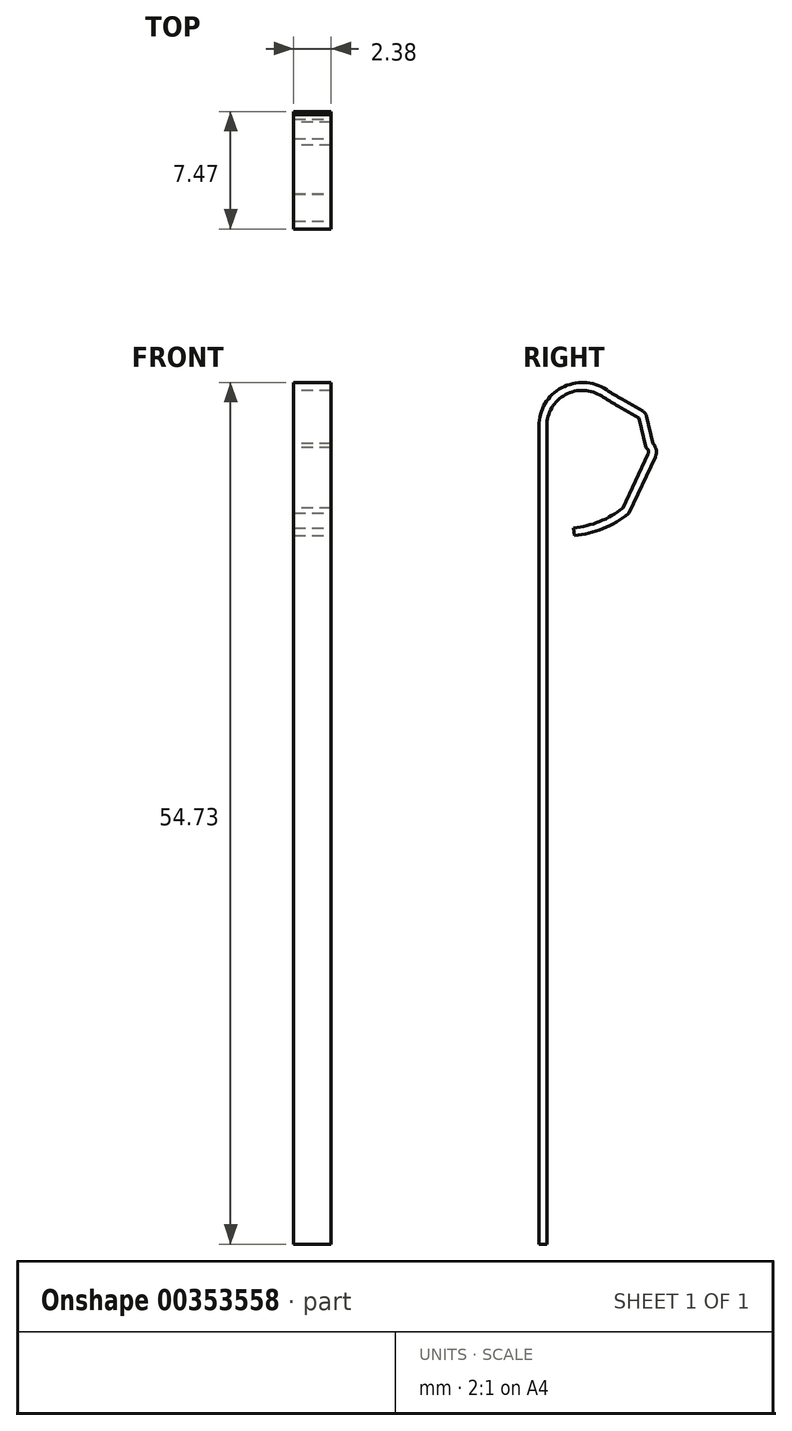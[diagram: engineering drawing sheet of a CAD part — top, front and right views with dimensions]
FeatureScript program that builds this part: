
annotation { "Feature Type Name" : "Feature", "Feature Type Description" : "" }
export const myFeature = defineFeature(function(context is Context, id is Id, definition is map)
    precondition{}
    {
        {
            var Q0;
            Q0=qCreatedBy(makeId("Top.planeOp"),FACE);
            var sketch = newSketch(context, id + "F0", { "sketchPlane" : qUnion([Q0])});
            skLineSegment(sketch, "E0.bottom", {"start": v(-1.2, 0.25) * mm, "end": v(1.2, 0.25) * mm});
            skLineSegment(sketch, "E0.top", {"start": v(-1.2, -0.25) * mm, "end": v(1.2, -0.25) * mm});
            skLineSegment(sketch, "E0.left", {"start": v(-1.2, 0.25) * mm, "end": v(-1.2, -0.25) * mm});
            skLineSegment(sketch, "E0.right", {"start": v(1.2, 0.25) * mm, "end": v(1.2, -0.25) * mm});
            skPoint(sketch, "E0.middle", {"position": v(0, 0) * mm});
            skSolve(sketch);
        }
        {
            var Q0;
            Q0=qCreatedBy(makeId("Right.planeOp"),FACE);
            var sketch = newSketch(context, id + "F1", { "sketchPlane" : qUnion([Q0])});
            skLineSegment(sketch, "E1", {"start": v(0, 0) * mm, "end": v(0, 19.05) * mm});
            skLineSegment(sketch, "E2", {"start": v(0, 19.05) * mm, "end": v(0, 47.31) * mm});
            skLineSegment(sketch, "E3", {"start": v(0, 47.31) * mm, "end": v(0, 51.97) * mm});
            skArc(sketch, "E4", {"start": v(3.9, 54.07) * mm, "mid": v(1.32, 54.18) * mm, "end": v(0, 51.97) * mm});
            skArc(sketch, "E5", {"start": v(1.98, 45.25) * mm, "mid": v(3.73, 45.68) * mm, "end": v(5.28, 46.6) * mm});
            skLineSegment(sketch, "E6", {"start": v(6.91, 50.1) * mm, "end": v(5.28, 46.6) * mm});
            skPoint(sketch, "E7.visualSharp", {"position": v(7.07, 50.42) * mm});
            skArc(sketch, "E7.filletArc", {"start": v(6.91, 50.1) * mm, "mid": v(6.95, 50.44) * mm, "end": v(6.78, 50.73) * mm});
            skLineSegment(sketch, "E8", {"start": v(4.89, 53.46) * mm, "end": v(6.22, 52.7) * mm});
            skLineSegment(sketch, "E9", {"start": v(6.35, 52.53) * mm, "end": v(6.78, 50.73) * mm});
            skPoint(sketch, "E10.visualSharp", {"position": v(4.13, 53.89) * mm});
            skArc(sketch, "E10.filletArc", {"start": v(3.9, 54.07) * mm, "mid": v(4.39, 53.75) * mm, "end": v(4.89, 53.46) * mm});
            skPoint(sketch, "E11.visualSharp", {"position": v(6.32, 52.64) * mm});
            skArc(sketch, "E11.filletArc", {"start": v(6.35, 52.53) * mm, "mid": v(6.3, 52.62) * mm, "end": v(6.22, 52.7) * mm});
            skSolve(sketch);
        }
        {
            var Q0;
            Q0 = qSketchRegion(id + "F0", true);
            var Q1;
            Q1 = qConstructionFilter(qBodyType(qCreatedBy(id + "F1" ,EDGE), BodyType.WIRE), ConstructionObject.NO);
            sweep(context, id + "F2", {"profiles" : qUnion([Q0]), "path" : qUnion([Q1])});
        }
    });
